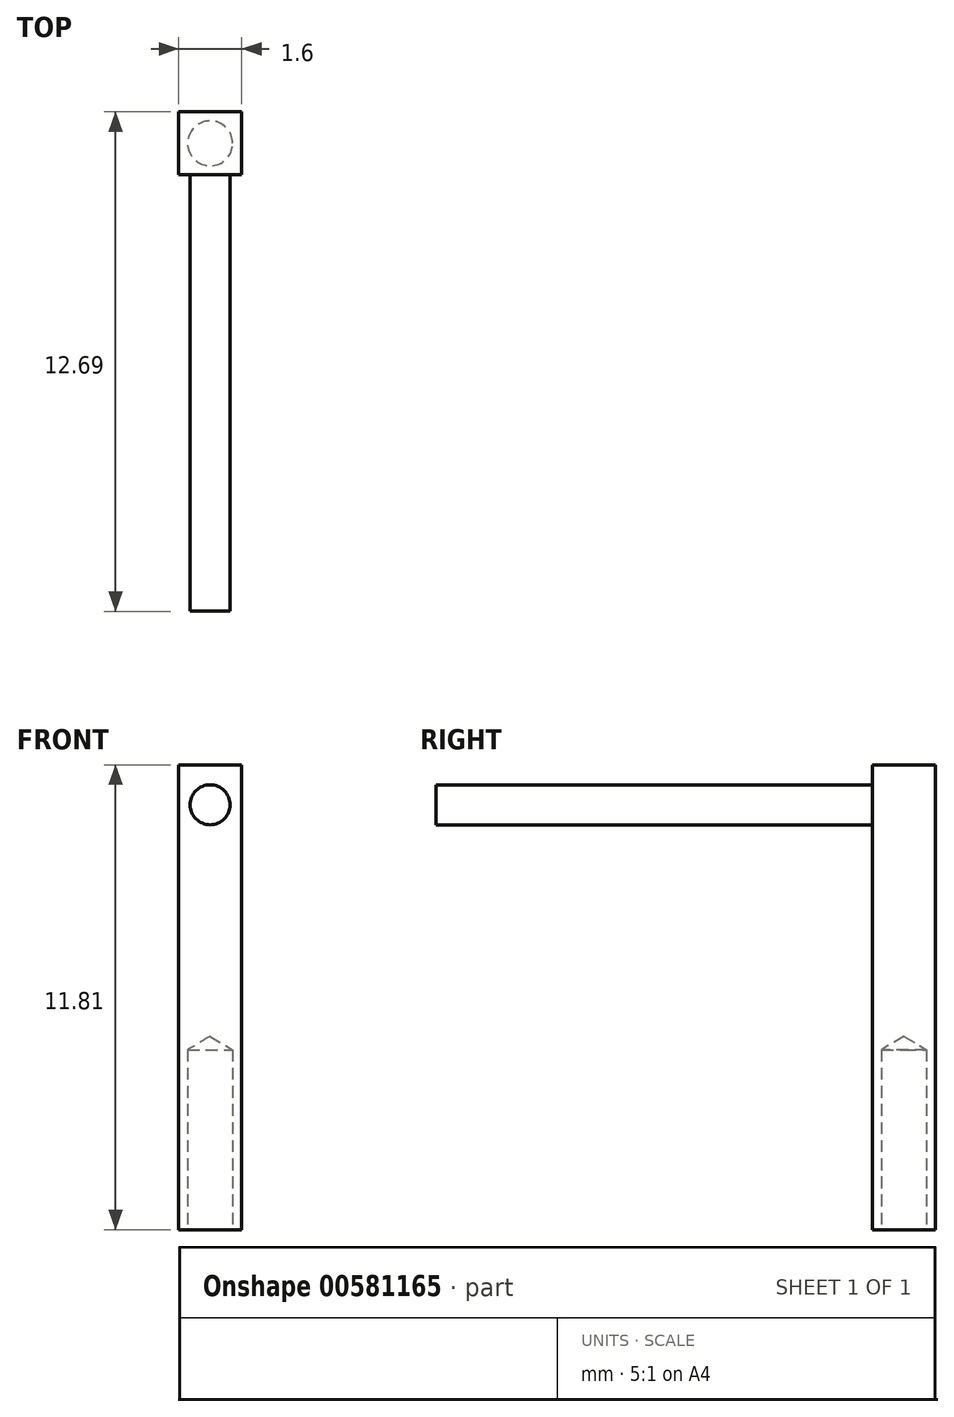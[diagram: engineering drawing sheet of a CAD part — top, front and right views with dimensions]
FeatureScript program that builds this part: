
annotation { "Feature Type Name" : "Feature", "Feature Type Description" : "" }
export const myFeature = defineFeature(function(context is Context, id is Id, definition is map)
    precondition{}
    {
        {
            var Q0;
            Q0=qCreatedBy(makeId("Top.planeOp"),FACE);
            var sketch = newSketch(context, id + "F0", { "sketchPlane" : qUnion([Q0])});
            skLineSegment(sketch, "E0.bottom", {"start": v(0.8, 0.8) * mm, "end": v(-0.8, 0.8) * mm});
            skLineSegment(sketch, "E0.top", {"start": v(0.8, -0.8) * mm, "end": v(-0.8, -0.8) * mm});
            skLineSegment(sketch, "E0.left", {"start": v(0.8, 0.8) * mm, "end": v(0.8, -0.8) * mm});
            skLineSegment(sketch, "E0.right", {"start": v(-0.8, 0.8) * mm, "end": v(-0.8, -0.8) * mm});
            skPoint(sketch, "E0.middle", {"position": v(0, 0) * mm});
            skSolve(sketch);
        }
        {
            var Q0;
            Q0 = qSketchRegion(id + "F0", true);
            extrude(context, id + "F1", {"entities" : qUnion([Q0]), "depth" : 11.8 * mm, "offsetDistance" : 25.4 * mm});
        }
        {
            var Q0;
            Q0=makeQuery(id+"F1.opExtrude","SWEPT_FACE",FACE,{"disambiguationData":[OSD([sQuery(id+"F0.wireOp",EDGE,"E0.top")])]});
            var sketch = newSketch(context, id + "F2", { "sketchPlane" : qUnion([Q0])});
            skPoint(sketch, "E1", {"position": v(0, 10.8) * mm});
            skCircle(sketch, "E2", {"center": v(0, 10.8) * mm, "radius": 0.5 * mm});
            skSolve(sketch);
        }
        {
            var Q0;
            Q0 = qSketchRegion(id + "F2", true);
            extrude(context, id + "F3", {"entities" : qUnion([Q0]), "operationType" : NewBodyOperationType.ADD, "depth" : 11.1 * mm, "offsetDistance" : 25.4 * mm});
        }
        {
            var Q0;
            Q0=makeQuery(id+"F1.opExtrude","CAP_FACE",FACE,{"disambiguationData":[OSD([sQuery(id+"F0.wireOp",EDGE,"E0.bottom"),sQuery(id+"F0.wireOp",EDGE,"E0.top"),sQuery(id+"F0.wireOp",EDGE,"E0.left"),sQuery(id+"F0.wireOp",EDGE,"E0.right")])],"isStart":true});
            var sketch = newSketch(context, id + "F4", { "sketchPlane" : qUnion([Q0])});
            skPoint(sketch, "E3", {"position": v(0, 0) * mm});
            skSolve(sketch);
        }
        {
            var Q0;
            Q0=sQuery(id+"F4.wireOp",VERTEX,"E3");
            var Q1;
            Q1=makeQuery(id+"F1.opExtrude","SWEPT_BODY",BODY,{"disambiguationData":[OSD([sQuery(id+"F0.wireOp",EDGE,"E0.bottom"),sQuery(id+"F0.wireOp",EDGE,"E0.top"),sQuery(id+"F0.wireOp",EDGE,"E0.left"),sQuery(id+"F0.wireOp",EDGE,"E0.right")])]});
            hole(context, id + "F5", {"style" : HoleStyle.SIMPLE, "endStyle" : HoleEndStyle.BLIND, "holeDiameter" : 1.14 * mm, "majorDiameter" : 6.35 * mm, "holeDepth" : 4.57 * mm, "isTappedThrough" : true, "tappedDepth" : 12.7 * mm, "tapClearance" : 3, "startFromSketch" : true, "locations" : qUnion([Q0]), "scope" : qUnion([Q1])});
        }
    });
